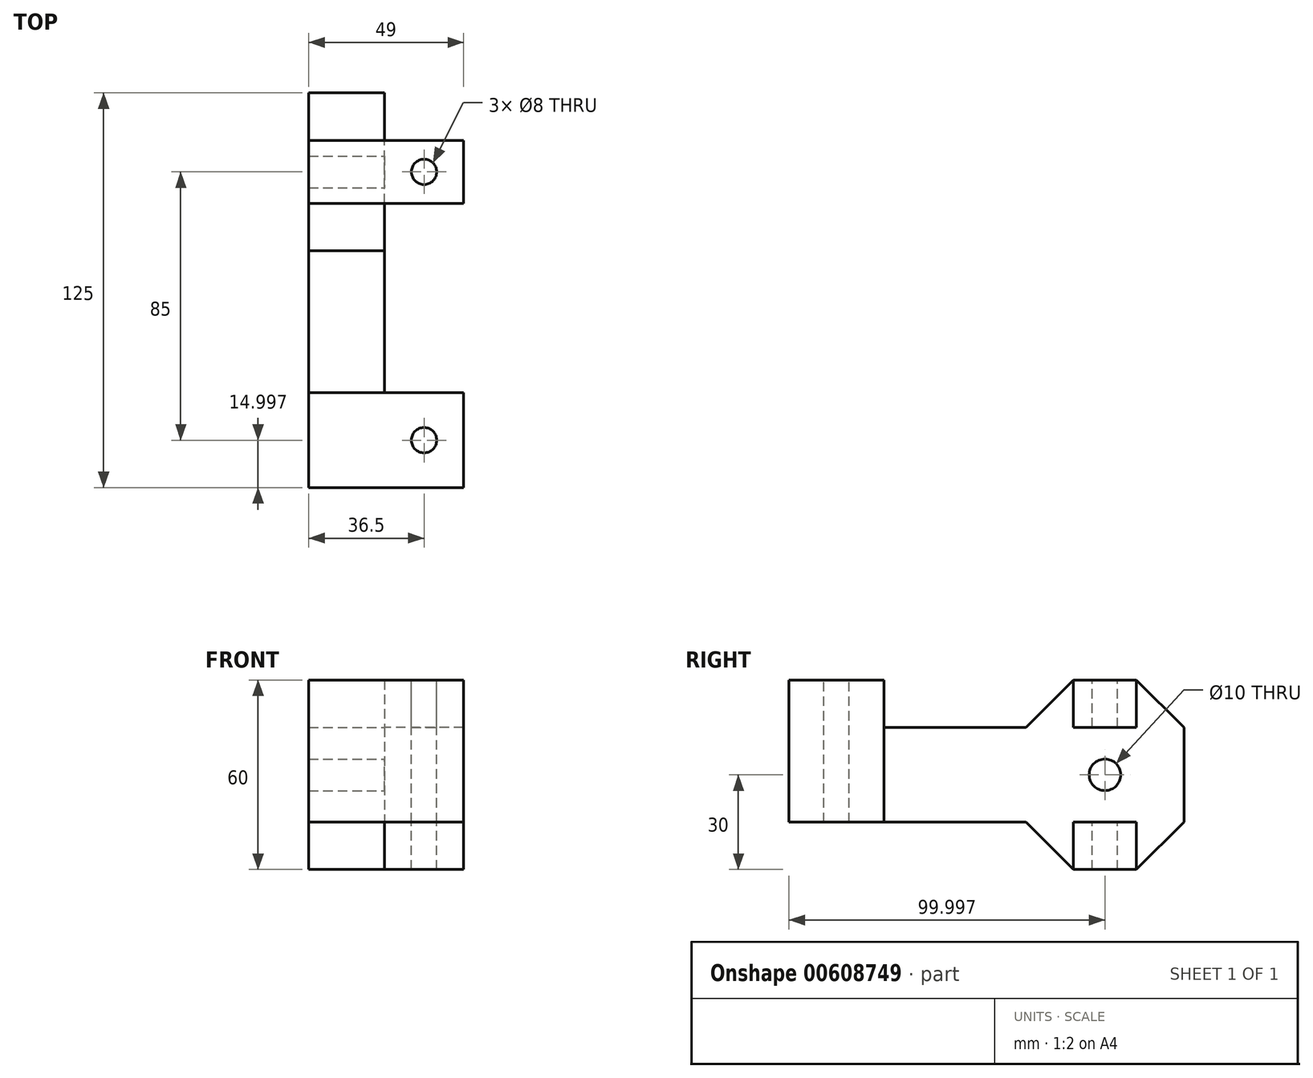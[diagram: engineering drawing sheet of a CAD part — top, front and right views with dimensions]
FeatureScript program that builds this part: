
annotation { "Feature Type Name" : "Feature", "Feature Type Description" : "" }
export const myFeature = defineFeature(function(context is Context, id is Id, definition is map)
    precondition{}
    {
        {
            var Q0;
            Q0=qCreatedBy(makeId("Right.planeOp"),FACE);
            var sketch = newSketch(context, id + "F0", { "sketchPlane" : qUnion([Q0])});
            skCircle(sketch, "E0", {"center": v(9.17, 2.5) * mm, "radius": 5 * mm});
            skLineSegment(sketch, "E1.0", {"start": v(19.17, -27.5) * mm, "end": v(-0.83, -27.5) * mm});
            skLineSegment(sketch, "E1.1", {"start": v(-0.83, -27.5) * mm, "end": v(-15.83, -12.5) * mm});
            skLineSegment(sketch, "E1.3", {"start": v(-15.83, 17.5) * mm, "end": v(-0.83, 32.5) * mm});
            skLineSegment(sketch, "E1.4", {"start": v(-0.83, 32.5) * mm, "end": v(19.17, 32.5) * mm});
            skLineSegment(sketch, "E1.5", {"start": v(19.17, 32.5) * mm, "end": v(34.17, 17.5) * mm});
            skLineSegment(sketch, "E1.6", {"start": v(34.17, 17.5) * mm, "end": v(34.17, -12.5) * mm});
            skLineSegment(sketch, "E1.7", {"start": v(34.17, -12.5) * mm, "end": v(19.17, -27.5) * mm});
            skPoint(sketch, "E1.0.midPoint", {"position": v(9.17, -27.5) * mm});
            skLineSegment(sketch, "E2", {"start": v(-15.83, 17.5) * mm, "end": v(-90.83, 17.5) * mm});
            skLineSegment(sketch, "E3", {"start": v(-90.83, 17.5) * mm, "end": v(-90.83, -12.5) * mm});
            skLineSegment(sketch, "E4", {"start": v(-90.83, -12.5) * mm, "end": v(-15.83, -12.5) * mm});
            skSolve(sketch);
        }
        {
            var Q0;
            Q0=makeQuery(id+"F0.imprint","IMPRINT",FACE,{"disambiguationData":[TD([[makeQuery(id+"F0.imprint","IMPRINT",EDGE,{"derivedFrom":sQuery(id+"F0.wireOp",EDGE,"E0")}),-1.0]])]});
            extrude(context, id + "F1", {"entities" : qUnion([Q0]), "oppositeDirection" : true, "depth" : 24 * mm, "offsetDistance" : 25 * mm});
        }
        {
            var Q0;
            Q0=makeQuery(id+"F1.opExtrude","CAP_FACE",FACE,{"disambiguationData":[OSD([sQuery(id+"F0.wireOp",EDGE,"E0"),sQuery(id+"F0.wireOp",EDGE,"E1.0"),sQuery(id+"F0.wireOp",EDGE,"E1.1"),sQuery(id+"F0.wireOp",EDGE,"E1.3"),sQuery(id+"F0.wireOp",EDGE,"E1.4"),sQuery(id+"F0.wireOp",EDGE,"E1.5"),sQuery(id+"F0.wireOp",EDGE,"E1.6"),sQuery(id+"F0.wireOp",EDGE,"E1.7"),sQuery(id+"F0.wireOp",EDGE,"E2"),sQuery(id+"F0.wireOp",EDGE,"E3"),sQuery(id+"F0.wireOp",EDGE,"E4")])],"isStart":true});
            var sketch = newSketch(context, id + "F2", { "sketchPlane" : qUnion([Q0])});
            skLineSegment(sketch, "E5", {"start": v(-0.83, 32.5) * mm, "end": v(19.17, 32.5) * mm});
            skLineSegment(sketch, "E6", {"start": v(19.17, 32.5) * mm, "end": v(19.17, 17.5) * mm});
            skLineSegment(sketch, "E7", {"start": v(19.17, 17.5) * mm, "end": v(-0.83, 17.5) * mm});
            skLineSegment(sketch, "E8", {"start": v(-0.83, 17.5) * mm, "end": v(-0.83, 32.5) * mm});
            skLineSegment(sketch, "E9", {"start": v(-0.83, -12.5) * mm, "end": v(19.17, -12.5) * mm});
            skLineSegment(sketch, "E10", {"start": v(19.17, -12.5) * mm, "end": v(19.17, -27.5) * mm});
            skLineSegment(sketch, "E11", {"start": v(19.17, -27.5) * mm, "end": v(-0.83, -27.5) * mm});
            skLineSegment(sketch, "E12", {"start": v(-0.83, -27.5) * mm, "end": v(-0.83, -12.5) * mm});
            skLineSegment(sketch, "E13.bottom", {"start": v(-90.83, 17.5) * mm, "end": v(-60.83, 17.5) * mm});
            skLineSegment(sketch, "E13.top", {"start": v(-90.83, -12.5) * mm, "end": v(-60.83, -12.5) * mm});
            skLineSegment(sketch, "E13.left", {"start": v(-90.83, 17.5) * mm, "end": v(-90.83, -12.5) * mm});
            skLineSegment(sketch, "E13.right", {"start": v(-60.83, 17.5) * mm, "end": v(-60.83, -12.5) * mm});
            skSolve(sketch);
        }
        {
            var Q0;
            Q0=makeQuery(id+"F2.imprint","IMPRINT",FACE,{"disambiguationData":[TD([[makeQuery(id+"F2.imprint","IMPRINT",EDGE,{"derivedFrom":sQuery(id+"F2.wireOp",EDGE,"E13.bottom")}),1.0]])]});
            var Q1;
            Q1=makeQuery(id+"F2.imprint","IMPRINT",FACE,{"disambiguationData":[TD([[makeQuery(id+"F2.imprint","IMPRINT",EDGE,{"derivedFrom":sQuery(id+"F2.wireOp",EDGE,"E5")}),-1.0]])]});
            var Q2;
            Q2=makeQuery(id+"F2.imprint","IMPRINT",FACE,{"disambiguationData":[TD([[makeQuery(id+"F2.imprint","IMPRINT",EDGE,{"derivedFrom":sQuery(id+"F2.wireOp",EDGE,"E9")}),-1.0]])]});
            extrude(context, id + "F3", {"entities" : qUnion([Q0, Q1, Q2]), "operationType" : NewBodyOperationType.ADD, "depth" : 25 * mm, "offsetDistance" : 25 * mm});
        }
        {
            var Q0;
            Q0=makeQuery(id+"F3.boolean.opBoolean","MERGE",FACE,{"derivedFrom":[makeQuery(id+"F1.opExtrude","SWEPT_FACE",FACE,{"disambiguationData":[OSD([sQuery(id+"F0.wireOp",EDGE,"E1.4")])]}),makeQuery(id+"F3.opExtrude","SWEPT_FACE",FACE,{"disambiguationData":[OSD([sQuery(id+"F2.wireOp",EDGE,"E5")])]})]});
            var sketch = newSketch(context, id + "F4", { "sketchPlane" : qUnion([Q0])});
            skCircle(sketch, "E14", {"center": v(12.5, 9.17) * mm, "radius": 4 * mm});
            skSolve(sketch);
        }
        {
            var Q0;
            Q0=sQuery(id+"F4.wireOp",VERTEX,"E14.center");
            var Q1;
            Q1=makeQuery(id+"F1.opExtrude","SWEPT_BODY",BODY,{"disambiguationData":[OSD([sQuery(id+"F0.wireOp",EDGE,"E0"),sQuery(id+"F0.wireOp",EDGE,"E1.0"),sQuery(id+"F0.wireOp",EDGE,"E1.1"),sQuery(id+"F0.wireOp",EDGE,"E1.3"),sQuery(id+"F0.wireOp",EDGE,"E1.4"),sQuery(id+"F0.wireOp",EDGE,"E1.5"),sQuery(id+"F0.wireOp",EDGE,"E1.6"),sQuery(id+"F0.wireOp",EDGE,"E1.7"),sQuery(id+"F0.wireOp",EDGE,"E2"),sQuery(id+"F0.wireOp",EDGE,"E3"),sQuery(id+"F0.wireOp",EDGE,"E4")])]});
            hole(context, id + "F5", {"style" : HoleStyle.SIMPLE, "endStyle" : HoleEndStyle.THROUGH, "holeDiameter" : 8 * mm, "majorDiameter" : 5 * mm, "isTappedThrough" : true, "tappedDepth" : 12 * mm, "tapClearance" : 3, "locations" : qUnion([Q0]), "scope" : qUnion([Q1])});
        }
        {
            var Q0;
            Q0=makeQuery(id+"F1.opExtrude","SWEPT_FACE",FACE,{"disambiguationData":[OSD([sQuery(id+"F0.wireOp",EDGE,"E2")])]});
            var sketch = newSketch(context, id + "F6", { "sketchPlane" : qUnion([Q0])});
            skCircle(sketch, "E15", {"center": v(12.5, -75.83) * mm, "radius": 4 * mm});
            skLineSegment(sketch, "E16.bottom", {"start": v(-24, -90.83) * mm, "end": v(25, -90.83) * mm});
            skLineSegment(sketch, "E16.top", {"start": v(-24, -60.83) * mm, "end": v(25, -60.83) * mm});
            skLineSegment(sketch, "E16.left", {"start": v(-24, -90.83) * mm, "end": v(-24, -60.83) * mm});
            skLineSegment(sketch, "E16.right", {"start": v(25, -90.83) * mm, "end": v(25, -60.83) * mm});
            skSolve(sketch);
        }
        {
            var Q0;
            Q0=sQuery(id+"F6.wireOp",VERTEX,"E15.center");
            var Q1;
            Q1=makeQuery(id+"F1.opExtrude","SWEPT_BODY",BODY,{"disambiguationData":[OSD([sQuery(id+"F0.wireOp",EDGE,"E0"),sQuery(id+"F0.wireOp",EDGE,"E1.0"),sQuery(id+"F0.wireOp",EDGE,"E1.1"),sQuery(id+"F0.wireOp",EDGE,"E1.3"),sQuery(id+"F0.wireOp",EDGE,"E1.4"),sQuery(id+"F0.wireOp",EDGE,"E1.5"),sQuery(id+"F0.wireOp",EDGE,"E1.6"),sQuery(id+"F0.wireOp",EDGE,"E1.7"),sQuery(id+"F0.wireOp",EDGE,"E2"),sQuery(id+"F0.wireOp",EDGE,"E3"),sQuery(id+"F0.wireOp",EDGE,"E4")])]});
            hole(context, id + "F7", {"style" : HoleStyle.SIMPLE, "endStyle" : HoleEndStyle.THROUGH, "holeDiameter" : 8 * mm, "majorDiameter" : 5 * mm, "isTappedThrough" : true, "tappedDepth" : 12 * mm, "tapClearance" : 3, "locations" : qUnion([Q0]), "scope" : qUnion([Q1])});
        }
        {
            var Q0;
            Q0=makeQuery(id+"F6.imprint","IMPRINT",FACE,{"disambiguationData":[TD([[makeQuery(id+"F6.imprint","IMPRINT",EDGE,{"derivedFrom":sQuery(id+"F6.wireOp",EDGE,"E15")}),-1.0]])]});
            extrude(context, id + "F8", {"entities" : qUnion([Q0]), "operationType" : NewBodyOperationType.ADD, "depth" : 15 * mm, "offsetDistance" : 25 * mm});
        }
    });
